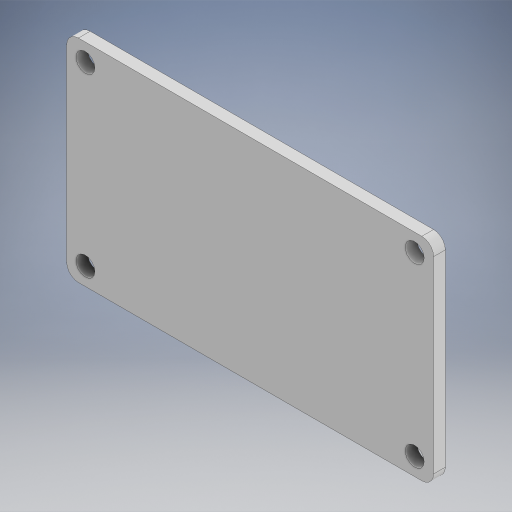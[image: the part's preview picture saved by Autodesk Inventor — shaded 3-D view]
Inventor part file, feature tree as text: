
AUTODESK INVENTOR PART (.ipt)
format: ipt  version: 2024.2 (Build 282272000, 272)  size: 232,448 bytes
history: native  units: in
note: dims shown in document units (in); Inventor stores cm internally (conversion verified against a paired STEP export)
features: extrude x1, fillet x1, sketch x1
ambient origin geometry x8: Origin, YZ Plane, XZ Plane, XY Plane, X Axis, Y Axis, Z Axis, Center Point
bodies: Solid1 (feature_tree)
feature tree (3):
  extrude  "Extrusion1"  Depth=0.125in
  fillet  "Fillet1"  Radius=3.5in
  sketch  "Sketch1"  dims[d0=0.202in d1=0.202in d2=3.5in d3=0.7874in d5=1.875in d6=0.3937in d8=1.0in d10=3.9in d11=2.25in d12=0.125in d13=0.0in d14=0.125in]
